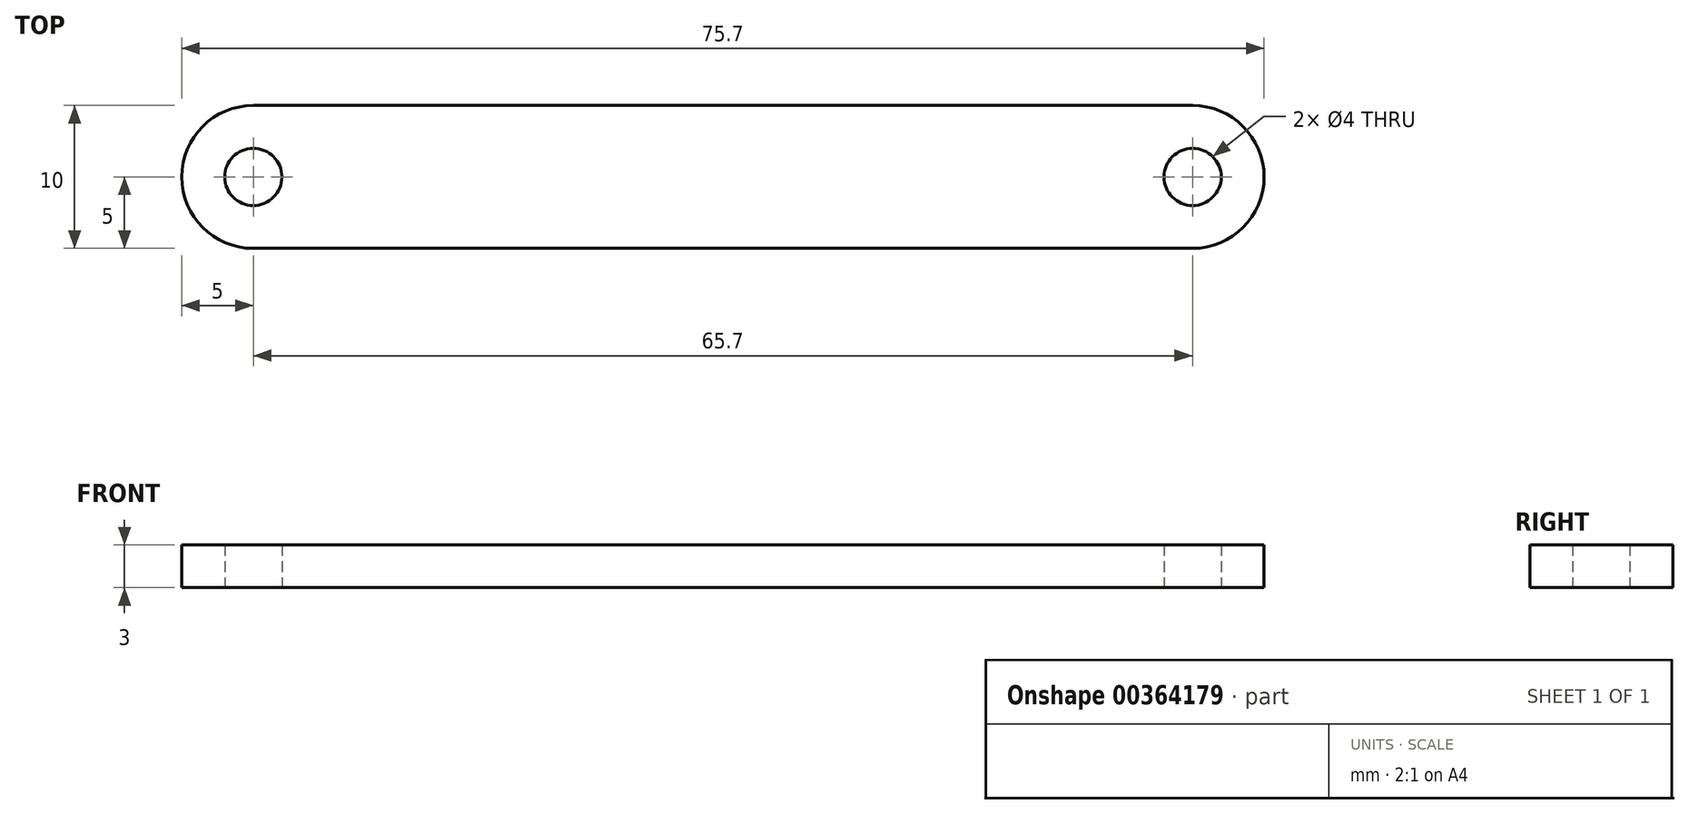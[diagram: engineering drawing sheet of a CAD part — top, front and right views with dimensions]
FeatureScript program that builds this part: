
annotation { "Feature Type Name" : "Feature", "Feature Type Description" : "" }
export const myFeature = defineFeature(function(context is Context, id is Id, definition is map)
    precondition{}
    {
        {
            var Q0;
            Q0=qCreatedBy(makeId("Top.planeOp"),FACE);
            var sketch = newSketch(context, id + "F0", { "sketchPlane" : qUnion([Q0])});
            skLineSegment(sketch, "E0.bottom", {"start": v(32.85, 5) * mm, "end": v(-32.85, 5) * mm});
            skLineSegment(sketch, "E0.top", {"start": v(32.85, -5) * mm, "end": v(-32.85, -5) * mm});
            skPoint(sketch, "E0.middle", {"position": v(0, 0) * mm});
            skCircle(sketch, "E1", {"center": v(-32.85, 0) * mm, "radius": 2 * mm});
            skCircle(sketch, "E2", {"center": v(32.85, 0) * mm, "radius": 2 * mm});
            skArc(sketch, "E3", {"start": v(-32.85, 5) * mm, "mid": v(-37.85, 0) * mm, "end": v(-32.85, -5) * mm});
            skArc(sketch, "E4", {"start": v(32.85, -5) * mm, "mid": v(37.85, 0) * mm, "end": v(32.85, 5) * mm});
            skSolve(sketch);
        }
        {
            var Q0;
            Q0=qSketchRegion(id+"F0",true);
            extrude(context, id + "F1", {"entities" : qUnion([Q0]), "depth" : 3 * mm});
        }
    });
